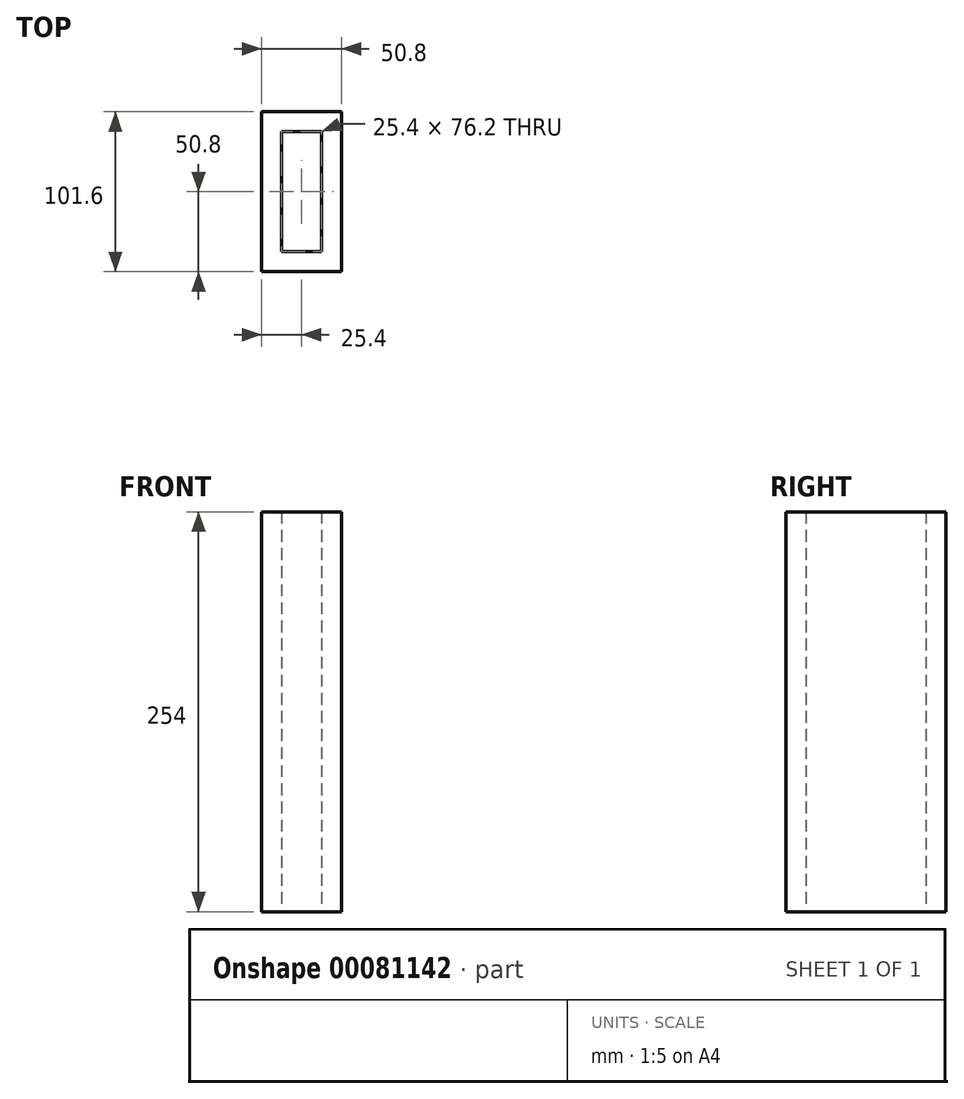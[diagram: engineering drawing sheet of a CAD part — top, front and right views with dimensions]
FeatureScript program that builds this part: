
annotation { "Feature Type Name" : "Feature", "Feature Type Description" : "" }
export const myFeature = defineFeature(function(context is Context, id is Id, definition is map)
    precondition{}
    {
        {
            var Q0;
            Q0=qCreatedBy(makeId("Top.planeOp"),FACE);
            var sketch = newSketch(context, id + "F0", { "sketchPlane" : qUnion([Q0])});
            skLineSegment(sketch, "E0.bottom", {"start": v(25.4, 50.8) * mm, "end": v(-25.4, 50.8) * mm});
            skLineSegment(sketch, "E0.top", {"start": v(25.4, -50.8) * mm, "end": v(-25.4, -50.8) * mm});
            skLineSegment(sketch, "E0.left", {"start": v(25.4, 50.8) * mm, "end": v(25.4, -50.8) * mm});
            skLineSegment(sketch, "E0.right", {"start": v(-25.4, 50.8) * mm, "end": v(-25.4, -50.8) * mm});
            skPoint(sketch, "E0.middle", {"position": v(0, 0) * mm});
            skLineSegment(sketch, "E1.bottom", {"start": v(-12.7, 38.1) * mm, "end": v(12.7, 38.1) * mm});
            skLineSegment(sketch, "E1.top", {"start": v(-12.7, -38.1) * mm, "end": v(12.7, -38.1) * mm});
            skLineSegment(sketch, "E1.left", {"start": v(-12.7, 38.1) * mm, "end": v(-12.7, -38.1) * mm});
            skLineSegment(sketch, "E1.right", {"start": v(12.7, 38.1) * mm, "end": v(12.7, -38.1) * mm});
            skSolve(sketch);
        }
        {
            var Q0;
            Q0=makeQuery(id+"F0.imprint","IMPRINT",FACE,{"disambiguationData":[TD([[makeQuery(id+"F0.imprint","IMPRINT",EDGE,{"derivedFrom":sQuery(id+"F0.wireOp",EDGE,"E0.bottom")}),1.0]])]});
            extrude(context, id + "F1", {"entities" : qUnion([Q0]), "depth" : 254 * mm});
        }
    });
